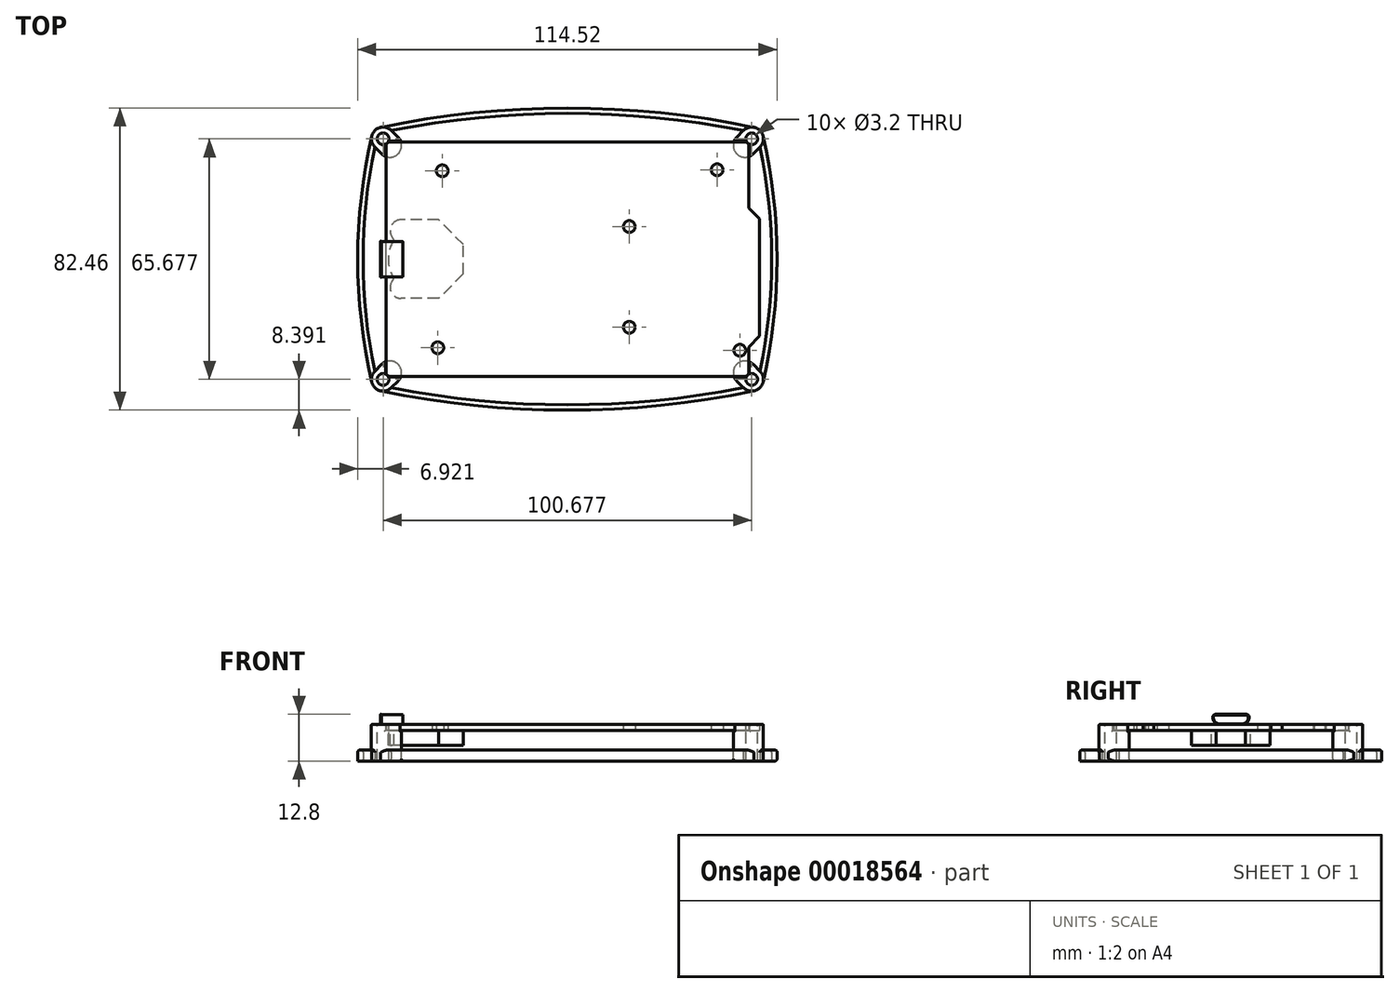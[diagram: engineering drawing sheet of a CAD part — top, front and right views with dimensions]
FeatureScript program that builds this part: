
annotation { "Feature Type Name" : "Feature", "Feature Type Description" : "" }
export const myFeature = defineFeature(function(context is Context, id is Id, definition is map)
    precondition{}
    {
        {
            var Q0;
            Q0=qCreatedBy(makeId("Top.planeOp"),FACE);
            var sketch = newSketch(context, id + "F0", { "sketchPlane" : qUnion([Q0])});
            skLineSegment(sketch, "E0.rect.bottom", {"start": v(48.5, -32) * mm, "end": v(-48.5, -32) * mm});
            skLineSegment(sketch, "E0.rect.top", {"start": v(48.5, 32) * mm, "end": v(-48.5, 32) * mm});
            skLineSegment(sketch, "E0.rect.left", {"start": v(49.5, -31) * mm, "end": v(49.5, -24) * mm});
            skLineSegment(sketch, "E0.rect.right", {"start": v(-49.5, -31) * mm, "end": v(-49.5, 31) * mm});
            skPoint(sketch, "E0.rect.middle", {"position": v(0, 0) * mm});
            skLineSegment(sketch, "E1", {"start": v(49.5, 14) * mm, "end": v(52.5, 11) * mm});
            skLineSegment(sketch, "E2", {"start": v(52.5, 11) * mm, "end": v(52.5, -21) * mm});
            skLineSegment(sketch, "E3", {"start": v(52.5, -21) * mm, "end": v(49.5, -24) * mm});
            skLineSegment(sketch, "E4.trimOffspring", {"start": v(49.5, 14) * mm, "end": v(49.5, 31) * mm});
            skPoint(sketch, "E5.visualSharp", {"position": v(-49.5, 32) * mm});
            skArc(sketch, "E5.filletArc", {"start": v(-48.5, 32) * mm, "mid": v(-49.2, 31.7) * mm, "end": v(-49.5, 31) * mm});
            skPoint(sketch, "E6.visualSharp", {"position": v(49.5, 32) * mm});
            skArc(sketch, "E6.filletArc", {"start": v(49.5, 31) * mm, "mid": v(49.2, 31.7) * mm, "end": v(48.5, 32) * mm});
            skPoint(sketch, "E7.visualSharp", {"position": v(49.5, -32) * mm});
            skArc(sketch, "E7.filletArc", {"start": v(48.5, -32) * mm, "mid": v(49.2, -31.7) * mm, "end": v(49.5, -31) * mm});
            skPoint(sketch, "E8.visualSharp", {"position": v(-49.5, -32) * mm});
            skArc(sketch, "E8.filletArc", {"start": v(-49.5, -31) * mm, "mid": v(-49.2, -31.7) * mm, "end": v(-48.5, -32) * mm});
            skCircle(sketch, "E9", {"center": v(-34.2, 24.1) * mm, "radius": 1.6 * mm});
            skCircle(sketch, "E10", {"center": v(40.9, 24.4) * mm, "radius": 1.6 * mm});
            skCircle(sketch, "E11", {"center": v(47.1, -24.9) * mm, "radius": 1.6 * mm});
            skCircle(sketch, "E12", {"center": v(16.9, -18.6) * mm, "radius": 1.6 * mm});
            skCircle(sketch, "E13", {"center": v(16.9, 8.9) * mm, "radius": 1.6 * mm});
            skCircle(sketch, "E14", {"center": v(-35.4, -24.2) * mm, "radius": 1.6 * mm});
            skSolve(sketch);
        }
        {
            var Q0;
            Q0 = qSketchRegion(id + "F0", true);
            extrude(context, id + "F1", {"entities" : qUnion([Q0]), "depth" : 1.7 * mm});
        }
        {
            var Q0;
            Q0=qCreatedBy(makeId("Right.planeOp"),FACE);
            cPlane(context, id + "F2", {"entities" : qUnion([Q0]), "cplaneType" : CPlaneType.OFFSET, "offset" : 50 * mm, "oppositeDirection" : true, "width" : 150 * mm, "height" : 150 * mm});
        }
        {
            var Q0;
            Q0=qCreatedBy(makeId("Front.planeOp"),FACE);
            var sketch = newSketch(context, id + "F3", { "sketchPlane" : qUnion([Q0])});
            skLineSegment(sketch, "E15", {"start": v(-50.99, 4.41) * mm, "end": v(-50.9, 4.33) * mm});
            skLineSegment(sketch, "E16", {"start": v(-50.83, 4.3) * mm, "end": v(-45, 4.3) * mm});
            skLineSegment(sketch, "E17", {"start": v(-50.91, 4.49) * mm, "end": v(-50.83, 4.4) * mm});
            skLineSegment(sketch, "E18", {"start": v(-50.83, 4.4) * mm, "end": v(-45.1, 4.4) * mm});
            skArc(sketch, "E19", {"start": v(-50.91, 4.49) * mm, "mid": v(-50.99, 4.49) * mm, "end": v(-50.99, 4.41) * mm});
            skPoint(sketch, "E20.visualSharp", {"position": v(-50.87, 4.3) * mm});
            skArc(sketch, "E20.filletArc", {"start": v(-50.9, 4.33) * mm, "mid": v(-50.87, 4.3) * mm, "end": v(-50.83, 4.3) * mm});
            skPoint(sketch, "E21.visualSharp", {"position": v(-45, 4.4) * mm});
            skArc(sketch, "E21.filletArc", {"start": v(-45, 4.3) * mm, "mid": v(-45.03, 4.37) * mm, "end": v(-45.1, 4.4) * mm});
            skSolve(sketch);
        }
        {
            var Q0;
            Q0=qCreatedBy(id+"F2.planeOp",FACE);
            var sketch = newSketch(context, id + "F4", { "sketchPlane" : qUnion([Q0])});
            skPoint(sketch, "E22.0", {"position": v(0, 4.41) * mm});
            skLineSegment(sketch, "E23", {"start": v(0, 4.41) * mm, "end": v(-4.06, 4.41) * mm});
            skArc(sketch, "E24", {"start": v(-4.06, 4.41) * mm, "mid": v(-4.63, 4.18) * mm, "end": v(-4.87, 3.6) * mm});
            skLineSegment(sketch, "E25", {"start": v(0, 4.41) * mm, "end": v(0, 1.7) * mm, "construction": true});
            skLineSegment(sketch, "E26", {"start": v(0, 1.7) * mm, "end": v(-2.98, 1.7) * mm});
            skArc(sketch, "E27", {"start": v(-4.87, 3.6) * mm, "mid": v(-4.32, 2.26) * mm, "end": v(-2.98, 1.7) * mm});
            skLineSegment(sketch, "E28.MirrorCS", {"start": v(0, 4.41) * mm, "end": v(4.06, 4.41) * mm});
            skArc(sketch, "E29.MirrorCS", {"start": v(4.06, 4.41) * mm, "mid": v(4.63, 4.18) * mm, "end": v(4.87, 3.6) * mm});
            skArc(sketch, "E30.MirrorCS", {"start": v(4.87, 3.6) * mm, "mid": v(4.32, 2.26) * mm, "end": v(2.98, 1.7) * mm});
            skLineSegment(sketch, "E31.MirrorCS", {"start": v(0, 1.7) * mm, "end": v(2.98, 1.7) * mm});
            skSolve(sketch);
        }
        {
            var Q0;
            Q0 = qSketchRegion(id + "F3", true);
            var Q1;
            Q1 = qConstructionFilter(qBodyType(qCreatedBy(id + "F4" ,EDGE), BodyType.WIRE), ConstructionObject.NO);
            sweep(context, id + "F5", {"profiles" : qUnion([Q0]), "path" : qUnion([Q1])});
        }
        {
            var Q0;
            Q0=makeQuery(id+"F1.opExtrude","CAP_FACE",FACE,{"disambiguationData":[OSD([sQuery(id+"F0.wireOp",EDGE,"E0.rect.bottom"),sQuery(id+"F0.wireOp",EDGE,"E0.rect.top"),sQuery(id+"F0.wireOp",EDGE,"E0.rect.left"),sQuery(id+"F0.wireOp",EDGE,"E0.rect.right"),sQuery(id+"F0.wireOp",EDGE,"E1"),sQuery(id+"F0.wireOp",EDGE,"E2"),sQuery(id+"F0.wireOp",EDGE,"E3"),sQuery(id+"F0.wireOp",EDGE,"E4.trimOffspring"),sQuery(id+"F0.wireOp",EDGE,"E5.filletArc"),sQuery(id+"F0.wireOp",EDGE,"E6.filletArc"),sQuery(id+"F0.wireOp",EDGE,"E7.filletArc"),sQuery(id+"F0.wireOp",EDGE,"E8.filletArc"),sQuery(id+"F0.wireOp",EDGE,"E9"),sQuery(id+"F0.wireOp",EDGE,"E10"),sQuery(id+"F0.wireOp",EDGE,"E11"),sQuery(id+"F0.wireOp",EDGE,"E12"),sQuery(id+"F0.wireOp",EDGE,"E13"),sQuery(id+"F0.wireOp",EDGE,"E14")])],"isStart":true});
            var sketch = newSketch(context, id + "F6", { "sketchPlane" : qUnion([Q0])});
            skLineSegment(sketch, "E32", {"start": v(0, 0) * mm, "end": v(-125.22, 0) * mm, "construction": true});
            skLineSegment(sketch, "E33", {"start": v(-28.41, 0) * mm, "end": v(-28.41, 4) * mm});
            skLineSegment(sketch, "E34", {"start": v(-28.41, 4) * mm, "end": v(-35.16, 10.75) * mm});
            skLineSegment(sketch, "E35", {"start": v(-35.16, 10.75) * mm, "end": v(-45.41, 10.75) * mm});
            skArc(sketch, "E36", {"start": v(-45.41, 10.75) * mm, "mid": v(-48.1, 9.1) * mm, "end": v(-47.82, 5.96) * mm});
            skArc(sketch, "E37", {"start": v(-47.38, 5.32) * mm, "mid": v(-47.6, 5.64) * mm, "end": v(-47.82, 5.96) * mm});
            skArc(sketch, "E38", {"start": v(-47.38, 5.32) * mm, "mid": v(-48.52, 2.77) * mm, "end": v(-48.91, 0) * mm});
            skArc(sketch, "E39.MirrorCS", {"start": v(-47.38, -5.32) * mm, "mid": v(-47.6, -5.64) * mm, "end": v(-47.82, -5.96) * mm});
            skArc(sketch, "E40.MirrorCS", {"start": v(-47.38, -5.32) * mm, "mid": v(-48.52, -2.77) * mm, "end": v(-48.91, 0) * mm});
            skLineSegment(sketch, "E41.MirrorCS", {"start": v(-28.41, 0) * mm, "end": v(-28.41, -4) * mm});
            skLineSegment(sketch, "E42.MirrorCS", {"start": v(-35.16, -10.75) * mm, "end": v(-45.41, -10.75) * mm});
            skLineSegment(sketch, "E43.MirrorCS", {"start": v(-28.41, -4) * mm, "end": v(-35.16, -10.75) * mm});
            skArc(sketch, "E44.MirrorCS", {"start": v(-45.41, -10.75) * mm, "mid": v(-48.1, -9.1) * mm, "end": v(-47.82, -5.96) * mm});
            skSolve(sketch);
        }
        {
            var Q0;
            Q0 = qSketchRegion(id + "F6", true);
            extrude(context, id + "F7", {"entities" : qUnion([Q0]), "operationType" : NewBodyOperationType.ADD, "depth" : 4 * mm});
        }
        {
            var Q0;
            Q0=makeQuery(id+"F1.opExtrude","CAP_FACE",FACE,{"disambiguationData":[OSD([sQuery(id+"F0.wireOp",EDGE,"E0.rect.bottom"),sQuery(id+"F0.wireOp",EDGE,"E0.rect.top"),sQuery(id+"F0.wireOp",EDGE,"E0.rect.left"),sQuery(id+"F0.wireOp",EDGE,"E0.rect.right"),sQuery(id+"F0.wireOp",EDGE,"E1"),sQuery(id+"F0.wireOp",EDGE,"E2"),sQuery(id+"F0.wireOp",EDGE,"E3"),sQuery(id+"F0.wireOp",EDGE,"E4.trimOffspring"),sQuery(id+"F0.wireOp",EDGE,"E5.filletArc"),sQuery(id+"F0.wireOp",EDGE,"E6.filletArc"),sQuery(id+"F0.wireOp",EDGE,"E7.filletArc"),sQuery(id+"F0.wireOp",EDGE,"E8.filletArc"),sQuery(id+"F0.wireOp",EDGE,"E9"),sQuery(id+"F0.wireOp",EDGE,"E10"),sQuery(id+"F0.wireOp",EDGE,"E11"),sQuery(id+"F0.wireOp",EDGE,"E12"),sQuery(id+"F0.wireOp",EDGE,"E13"),sQuery(id+"F0.wireOp",EDGE,"E14")])],"isStart":false});
            var sketch = newSketch(context, id + "F8", { "sketchPlane" : qUnion([Q0])});
            skCircle(sketch, "E45", {"center": v(50.34, 32.84) * mm, "radius": 1.6 * mm});
            skArc(sketch, "E46", {"start": v(52.6, 30.58) * mm, "mid": v(52.6, 35.1) * mm, "end": v(48.08, 35.1) * mm});
            skArc(sketch, "E47", {"start": v(46.24, 33.26) * mm, "mid": v(46.24, 28.74) * mm, "end": v(50.76, 28.74) * mm});
            skLineSegment(sketch, "E48", {"start": v(46.24, 33.26) * mm, "end": v(48.08, 35.1) * mm});
            skLineSegment(sketch, "E49", {"start": v(52.6, 30.58) * mm, "end": v(50.76, 28.74) * mm});
            skSolve(sketch);
        }
        {
            var Q0;
            Q0 = qSketchRegion(id + "F8", true);
            extrude(context, id + "F9", {"entities" : qUnion([Q0]), "oppositeDirection" : true, "depth" : 10 * mm});
        }
        {
            var Q0;
            Q0=makeQuery(id+"F1.opExtrude","SWEPT_BODY",BODY,{"disambiguationData":[OSD([sQuery(id+"F0.wireOp",EDGE,"E0.rect.bottom"),sQuery(id+"F0.wireOp",EDGE,"E0.rect.top"),sQuery(id+"F0.wireOp",EDGE,"E0.rect.left"),sQuery(id+"F0.wireOp",EDGE,"E0.rect.right"),sQuery(id+"F0.wireOp",EDGE,"E1"),sQuery(id+"F0.wireOp",EDGE,"E2"),sQuery(id+"F0.wireOp",EDGE,"E3"),sQuery(id+"F0.wireOp",EDGE,"E4.trimOffspring"),sQuery(id+"F0.wireOp",EDGE,"E5.filletArc"),sQuery(id+"F0.wireOp",EDGE,"E6.filletArc"),sQuery(id+"F0.wireOp",EDGE,"E7.filletArc"),sQuery(id+"F0.wireOp",EDGE,"E8.filletArc"),sQuery(id+"F0.wireOp",EDGE,"E9"),sQuery(id+"F0.wireOp",EDGE,"E10"),sQuery(id+"F0.wireOp",EDGE,"E11"),sQuery(id+"F0.wireOp",EDGE,"E12"),sQuery(id+"F0.wireOp",EDGE,"E13"),sQuery(id+"F0.wireOp",EDGE,"E14")])]});
            var Q1;
            Q1=makeQuery(id+"F9.opExtrude","SWEPT_BODY",BODY,{"disambiguationData":[OSD([sQuery(id+"F8.wireOp",EDGE,"E45"),sQuery(id+"F8.wireOp",EDGE,"E46"),sQuery(id+"F8.wireOp",EDGE,"E47"),sQuery(id+"F8.wireOp",EDGE,"E48"),sQuery(id+"F8.wireOp",EDGE,"E49")])]});
            var Q2;
            Q2=makeQuery(id+"F1.opExtrude","SWEPT_FACE",FACE,{"disambiguationData":[OSD([sQuery(id+"F0.wireOp",EDGE,"E4.trimOffspring")])]});
            var Q3;
            Q3=makeQuery(id+"F1.opExtrude","SWEPT_FACE",FACE,{"disambiguationData":[OSD([sQuery(id+"F0.wireOp",EDGE,"E0.rect.top")])]});
            var Q4;
            Q4=makeQuery(id+"F1.opExtrude","SWEPT_FACE",FACE,{"disambiguationData":[OSD([sQuery(id+"F0.wireOp",EDGE,"E6.filletArc")])]});
            booleanBodies(context, id + "F10", {"operationType" : BooleanOperationType.SUBTRACTION, "tools" : qUnion([Q0]), "targets" : qUnion([Q1]), "offset" : true, "entitiesToOffset" : qUnion([Q2, Q3, Q4]), "offsetDistance" : 0.2 * mm, "keepTools" : true});
        }
        {
            var Q0;
            Q0=makeQuery(id+"F9.opExtrude","CAP_EDGE",EDGE,{"disambiguationData":[OSD([sQuery(id+"F8.wireOp",EDGE,"E46")])],"isStart":true});
            var Q1;
            Q1=makeQuery(id+"F9.opExtrude","CAP_EDGE",EDGE,{"disambiguationData":[OSD([sQuery(id+"F8.wireOp",EDGE,"E45")])],"isStart":true});
            var Q2;
            Q2=makeQuery(id+"F10.tempBoolean.opBoolean","COPY",EDGE,{"derivedFrom":makeQuery(id+"F10.offsetTempBody.opPattern","COPY",EDGE,{"derivedFrom":makeQuery(id+"F1.opExtrude","CAP_EDGE",EDGE,{"disambiguationData":[OSD([sQuery(id+"F0.wireOp",EDGE,"E4.trimOffspring")])],"isStart":false}),"instanceName":"1"})});
            var Q3;
            Q3=makeQuery(id+"F10.tempBoolean.opBoolean","COPY",EDGE,{"derivedFrom":makeQuery(id+"F10.offsetTempBody.opPattern","COPY",EDGE,{"derivedFrom":makeQuery(id+"F1.opExtrude","CAP_EDGE",EDGE,{"disambiguationData":[OSD([sQuery(id+"F0.wireOp",EDGE,"E0.rect.top")])],"isStart":false}),"instanceName":"1"})});
            var Q4;
            Q4=makeQuery(id+"F10.tempBoolean.opBoolean","INTERSECT",EDGE,{"derivedFrom":[makeQuery(id+"F9.opExtrude","SWEPT_FACE",FACE,{"disambiguationData":[OSD([sQuery(id+"F8.wireOp",EDGE,"E45")])]}),makeQuery(id+"F10.offsetTempBody.opPattern","COPY",FACE,{"derivedFrom":makeQuery(id+"F1.opExtrude","CAP_FACE",FACE,{"disambiguationData":[OSD([sQuery(id+"F0.wireOp",EDGE,"E0.rect.bottom"),sQuery(id+"F0.wireOp",EDGE,"E0.rect.top"),sQuery(id+"F0.wireOp",EDGE,"E0.rect.left"),sQuery(id+"F0.wireOp",EDGE,"E0.rect.right"),sQuery(id+"F0.wireOp",EDGE,"E1"),sQuery(id+"F0.wireOp",EDGE,"E2"),sQuery(id+"F0.wireOp",EDGE,"E3"),sQuery(id+"F0.wireOp",EDGE,"E4.trimOffspring"),sQuery(id+"F0.wireOp",EDGE,"E5.filletArc"),sQuery(id+"F0.wireOp",EDGE,"E6.filletArc"),sQuery(id+"F0.wireOp",EDGE,"E7.filletArc"),sQuery(id+"F0.wireOp",EDGE,"E8.filletArc"),sQuery(id+"F0.wireOp",EDGE,"E9"),sQuery(id+"F0.wireOp",EDGE,"E10"),sQuery(id+"F0.wireOp",EDGE,"E11"),sQuery(id+"F0.wireOp",EDGE,"E12"),sQuery(id+"F0.wireOp",EDGE,"E13"),sQuery(id+"F0.wireOp",EDGE,"E14")])],"isStart":true}),"instanceName":"1"})]});
            var Q5;
            Q5=makeQuery(id+"F10.tempBoolean.opBoolean","INTERSECT",EDGE,{"derivedFrom":[makeQuery(id+"F9.opExtrude","SWEPT_FACE",FACE,{"disambiguationData":[OSD([sQuery(id+"F8.wireOp",EDGE,"E47")])]}),makeQuery(id+"F10.offsetTempBody.opPattern","COPY",FACE,{"derivedFrom":makeQuery(id+"F1.opExtrude","CAP_FACE",FACE,{"disambiguationData":[OSD([sQuery(id+"F0.wireOp",EDGE,"E0.rect.bottom"),sQuery(id+"F0.wireOp",EDGE,"E0.rect.top"),sQuery(id+"F0.wireOp",EDGE,"E0.rect.left"),sQuery(id+"F0.wireOp",EDGE,"E0.rect.right"),sQuery(id+"F0.wireOp",EDGE,"E1"),sQuery(id+"F0.wireOp",EDGE,"E2"),sQuery(id+"F0.wireOp",EDGE,"E3"),sQuery(id+"F0.wireOp",EDGE,"E4.trimOffspring"),sQuery(id+"F0.wireOp",EDGE,"E5.filletArc"),sQuery(id+"F0.wireOp",EDGE,"E6.filletArc"),sQuery(id+"F0.wireOp",EDGE,"E7.filletArc"),sQuery(id+"F0.wireOp",EDGE,"E8.filletArc"),sQuery(id+"F0.wireOp",EDGE,"E9"),sQuery(id+"F0.wireOp",EDGE,"E10"),sQuery(id+"F0.wireOp",EDGE,"E11"),sQuery(id+"F0.wireOp",EDGE,"E12"),sQuery(id+"F0.wireOp",EDGE,"E13"),sQuery(id+"F0.wireOp",EDGE,"E14")])],"isStart":true}),"instanceName":"1"})]});
            var Q6;
            Q6=makeQuery(id+"F10.tempBoolean.opBoolean","INTERSECT",EDGE,{"derivedFrom":[makeQuery(id+"F9.opExtrude","SWEPT_FACE",FACE,{"disambiguationData":[OSD([sQuery(id+"F8.wireOp",EDGE,"E47")])]}),makeQuery(id+"F10.offsetTempBody.opPattern","COPY",FACE,{"derivedFrom":makeQuery(id+"F1.opExtrude","SWEPT_FACE",FACE,{"disambiguationData":[OSD([sQuery(id+"F0.wireOp",EDGE,"E0.rect.top")])]}),"instanceName":"1"})]});
            var Q7;
            Q7=makeQuery(id+"F10.tempBoolean.opBoolean","INTERSECT",EDGE,{"derivedFrom":[makeQuery(id+"F9.opExtrude","SWEPT_FACE",FACE,{"disambiguationData":[OSD([sQuery(id+"F8.wireOp",EDGE,"E47")])]}),makeQuery(id+"F10.offsetTempBody.opPattern","COPY",FACE,{"derivedFrom":makeQuery(id+"F1.opExtrude","SWEPT_FACE",FACE,{"disambiguationData":[OSD([sQuery(id+"F0.wireOp",EDGE,"E4.trimOffspring")])]}),"instanceName":"1"})]});
            var Q8;
            Q8=makeQuery(id+"F9.opExtrude","CAP_EDGE",EDGE,{"disambiguationData":[OSD([sQuery(id+"F8.wireOp",EDGE,"E45")])],"isStart":false});
            var Q9;
            Q9=makeQuery(id+"F10.tempBoolean.opBoolean","INTERSECT",EDGE,{"disambiguationData":[OD(1.0)],"derivedFrom":[makeQuery(id+"F9.opExtrude","SWEPT_FACE",FACE,{"disambiguationData":[OSD([sQuery(id+"F8.wireOp",EDGE,"E45")])]}),makeQuery(id+"F10.offsetTempBody.opPattern","COPY",FACE,{"derivedFrom":makeQuery(id+"F1.opExtrude","SWEPT_FACE",FACE,{"disambiguationData":[OSD([sQuery(id+"F0.wireOp",EDGE,"E6.filletArc")])]}),"instanceName":"1"})]});
            var Q10;
            Q10=makeQuery(id+"F10.tempBoolean.opBoolean","INTERSECT",EDGE,{"disambiguationData":[OD(0.0)],"derivedFrom":[makeQuery(id+"F9.opExtrude","SWEPT_FACE",FACE,{"disambiguationData":[OSD([sQuery(id+"F8.wireOp",EDGE,"E45")])]}),makeQuery(id+"F10.offsetTempBody.opPattern","COPY",FACE,{"derivedFrom":makeQuery(id+"F1.opExtrude","SWEPT_FACE",FACE,{"disambiguationData":[OSD([sQuery(id+"F0.wireOp",EDGE,"E6.filletArc")])]}),"instanceName":"1"})]});
            fillet(context, id + "F11", {"entities" : qUnion([Q0, Q1, Q2, Q3, Q4, Q5, Q6, Q7, Q8, Q9, Q10]), "radius" : 0.25 * mm, "tangentPropagation" : true, "allowEdgeOverflow" : false});
        }
        {
            var Q0;
            Q0=makeQuery(id+"F9.opExtrude","SWEPT_BODY",BODY,{"disambiguationData":[OSD([sQuery(id+"F8.wireOp",EDGE,"E45"),sQuery(id+"F8.wireOp",EDGE,"E46"),sQuery(id+"F8.wireOp",EDGE,"E47"),sQuery(id+"F8.wireOp",EDGE,"E48"),sQuery(id+"F8.wireOp",EDGE,"E49")])]});
            var Q1;
            Q1=qCreatedBy(makeId("Front.planeOp"),FACE);
            mirror(context, id + "F12", {"entities" : qUnion([Q0]), "mirrorPlane" : qUnion([Q1])});
        }
        {
            var Q0;
            Q0=makeQuery(id+"F9.opExtrude","SWEPT_BODY",BODY,{"disambiguationData":[OSD([sQuery(id+"F8.wireOp",EDGE,"E45"),sQuery(id+"F8.wireOp",EDGE,"E46"),sQuery(id+"F8.wireOp",EDGE,"E47"),sQuery(id+"F8.wireOp",EDGE,"E48"),sQuery(id+"F8.wireOp",EDGE,"E49")])]});
            var Q1;
            Q1=makeQuery(id+"F12.opPattern","COPY",BODY,{"derivedFrom":makeQuery(id+"F9.opExtrude","SWEPT_BODY",BODY,{"disambiguationData":[OSD([sQuery(id+"F8.wireOp",EDGE,"E45"),sQuery(id+"F8.wireOp",EDGE,"E46"),sQuery(id+"F8.wireOp",EDGE,"E47"),sQuery(id+"F8.wireOp",EDGE,"E48"),sQuery(id+"F8.wireOp",EDGE,"E49")])]}),"instanceName":"1"});
            var Q2;
            Q2=qCreatedBy(makeId("Right.planeOp"),FACE);
            mirror(context, id + "F13", {"entities" : qUnion([Q0, Q1]), "mirrorPlane" : qUnion([Q2])});
        }
        {
            var Q0;
            Q0=makeQuery(id+"F13.opPattern","COPY",FACE,{"derivedFrom":makeQuery(id+"F9.opExtrude","CAP_FACE",FACE,{"disambiguationData":[OSD([sQuery(id+"F8.wireOp",EDGE,"E45"),sQuery(id+"F8.wireOp",EDGE,"E46"),sQuery(id+"F8.wireOp",EDGE,"E47"),sQuery(id+"F8.wireOp",EDGE,"E48"),sQuery(id+"F8.wireOp",EDGE,"E49")])],"isStart":false}),"instanceName":"1"});
            var sketch = newSketch(context, id + "F14", { "sketchPlane" : qUnion([Q0])});
            skLineSegment(sketch, "E50", {"start": v(0, 0) * mm, "end": v(-22.4, 0) * mm, "construction": true});
            skArc(sketch, "E51", {"start": v(-53.46, 33.55) * mm, "mid": v(-57.26, 0) * mm, "end": v(-53.46, -33.55) * mm});
            skArc(sketch, "E52", {"start": v(-52.6, 30.58) * mm, "mid": v(-55.78, 0) * mm, "end": v(-52.6, -30.58) * mm});
            skLineSegment(sketch, "E53", {"start": v(0, 0) * mm, "end": v(0, 25.87) * mm, "construction": true});
            skArc(sketch, "E54.0", {"start": v(-52.6, -30.58) * mm, "mid": v(-53.41, -31.95) * mm, "end": v(-53.46, -33.55) * mm});
            skArc(sketch, "E55.0", {"start": v(-52.6, 30.58) * mm, "mid": v(-53.41, 31.95) * mm, "end": v(-53.46, 33.55) * mm});
            skSolve(sketch);
        }
        {
            var Q0;
            Q0 = qSketchRegion(id + "F14", true);
            extrude(context, id + "F15", {"entities" : qUnion([Q0]), "oppositeDirection" : true, "depth" : 3 * mm});
        }
        {
            var Q0;
            Q0=makeQuery(id+"F13.opPattern","COPY",FACE,{"derivedFrom":makeQuery(id+"F9.opExtrude","CAP_FACE",FACE,{"disambiguationData":[OSD([sQuery(id+"F8.wireOp",EDGE,"E45"),sQuery(id+"F8.wireOp",EDGE,"E46"),sQuery(id+"F8.wireOp",EDGE,"E47"),sQuery(id+"F8.wireOp",EDGE,"E48"),sQuery(id+"F8.wireOp",EDGE,"E49")])],"isStart":false}),"instanceName":"1"});
            var sketch = newSketch(context, id + "F16", { "sketchPlane" : qUnion([Q0])});
            skLineSegment(sketch, "E56", {"start": v(0, 0) * mm, "end": v(-17.58, 0) * mm, "construction": true});
            skLineSegment(sketch, "E57", {"start": v(0, 14.8) * mm, "end": v(0, 0) * mm, "construction": true});
            skArc(sketch, "E58", {"start": v(51, 35.97) * mm, "mid": v(0, 41.23) * mm, "end": v(-51, 35.97) * mm});
            skArc(sketch, "E59", {"start": v(48.08, 35.1) * mm, "mid": v(0, 39.8) * mm, "end": v(-48.08, 35.1) * mm});
            skArc(sketch, "E60.0", {"start": v(-51, 35.97) * mm, "mid": v(-49.42, 35.9) * mm, "end": v(-48.08, 35.1) * mm});
            skArc(sketch, "E61.0", {"start": v(51, 35.97) * mm, "mid": v(49.42, 35.9) * mm, "end": v(48.08, 35.1) * mm});
            skSolve(sketch);
        }
        {
            var Q0;
            Q0 = qSketchRegion(id + "F16", true);
            extrude(context, id + "F17", {"entities" : qUnion([Q0]), "oppositeDirection" : true, "depth" : 3 * mm});
        }
        {
            var Q0;
            Q0=makeQuery(id+"F15.opExtrude","SWEPT_BODY",BODY,{"disambiguationData":[OSD([sQuery(id+"F14.wireOp",EDGE,"E51"),sQuery(id+"F14.wireOp",EDGE,"E52"),sQuery(id+"F14.wireOp",EDGE,"E54.0"),sQuery(id+"F14.wireOp",EDGE,"E55.0")])]});
            var Q1;
            Q1=qCreatedBy(makeId("Right.planeOp"),FACE);
            mirror(context, id + "F18", {"entities" : qUnion([Q0]), "mirrorPlane" : qUnion([Q1])});
        }
        {
            var Q0;
            Q0=makeQuery(id+"F17.opExtrude","SWEPT_BODY",BODY,{"disambiguationData":[OSD([sQuery(id+"F16.wireOp",EDGE,"E58"),sQuery(id+"F16.wireOp",EDGE,"E59"),sQuery(id+"F16.wireOp",EDGE,"E60.0"),sQuery(id+"F16.wireOp",EDGE,"E61.0")])]});
            var Q1;
            Q1=qCreatedBy(makeId("Front.planeOp"),FACE);
            mirror(context, id + "F19", {"entities" : qUnion([Q0]), "mirrorPlane" : qUnion([Q1])});
        }
        {
            var Q0;
            Q0=makeQuery(id+"F18.opPattern","COPY",EDGE,{"derivedFrom":makeQuery(id+"F15.opExtrude","CAP_EDGE",EDGE,{"disambiguationData":[OSD([sQuery(id+"F14.wireOp",EDGE,"E51")])],"isStart":true}),"instanceName":"1"});
            var Q1;
            Q1=makeQuery(id+"F19.opPattern","COPY",EDGE,{"derivedFrom":makeQuery(id+"F17.opExtrude","CAP_EDGE",EDGE,{"disambiguationData":[OSD([sQuery(id+"F16.wireOp",EDGE,"E59")])],"isStart":true}),"instanceName":"1"});
            var Q2;
            Q2=makeQuery(id+"F9.opExtrude","CAP_EDGE",EDGE,{"disambiguationData":[OSD([sQuery(id+"F8.wireOp",EDGE,"E48")])],"isStart":false});
            var Q3;
            Q3=makeQuery(id+"F18.opPattern","COPY",EDGE,{"derivedFrom":makeQuery(id+"F15.opExtrude","CAP_EDGE",EDGE,{"disambiguationData":[OSD([sQuery(id+"F14.wireOp",EDGE,"E52")])],"isStart":true}),"instanceName":"1"});
            var Q4;
            Q4=makeQuery(id+"F12.opPattern","COPY",EDGE,{"derivedFrom":makeQuery(id+"F9.opExtrude","CAP_EDGE",EDGE,{"disambiguationData":[OSD([sQuery(id+"F8.wireOp",EDGE,"E49")])],"isStart":false}),"instanceName":"1"});
            var Q5;
            Q5=makeQuery(id+"F17.opExtrude","CAP_EDGE",EDGE,{"disambiguationData":[OSD([sQuery(id+"F16.wireOp",EDGE,"E59")])],"isStart":true});
            var Q6;
            Q6=makeQuery(id+"F13.opPattern","COPY",EDGE,{"derivedFrom":makeQuery(id+"F12.opPattern","COPY",EDGE,{"derivedFrom":makeQuery(id+"F9.opExtrude","CAP_EDGE",EDGE,{"disambiguationData":[OSD([sQuery(id+"F8.wireOp",EDGE,"E48")])],"isStart":false}),"instanceName":"1"}),"instanceName":"1"});
            var Q7;
            Q7=makeQuery(id+"F15.opExtrude","CAP_EDGE",EDGE,{"disambiguationData":[OSD([sQuery(id+"F14.wireOp",EDGE,"E52")])],"isStart":true});
            var Q8;
            Q8=makeQuery(id+"F13.opPattern","COPY",EDGE,{"derivedFrom":makeQuery(id+"F9.opExtrude","CAP_EDGE",EDGE,{"disambiguationData":[OSD([sQuery(id+"F8.wireOp",EDGE,"E49")])],"isStart":false}),"instanceName":"1"});
            var Q9;
            Q9=makeQuery(id+"F17.opExtrude","CAP_EDGE",EDGE,{"disambiguationData":[OSD([sQuery(id+"F16.wireOp",EDGE,"E58")])],"isStart":false});
            var Q10;
            Q10=makeQuery(id+"F17.opExtrude","CAP_EDGE",EDGE,{"disambiguationData":[OSD([sQuery(id+"F16.wireOp",EDGE,"E59")])],"isStart":false});
            var Q11;
            Q11=makeQuery(id+"F15.opExtrude","CAP_EDGE",EDGE,{"disambiguationData":[OSD([sQuery(id+"F14.wireOp",EDGE,"E51")])],"isStart":false});
            var Q12;
            Q12=makeQuery(id+"F15.opExtrude","CAP_EDGE",EDGE,{"disambiguationData":[OSD([sQuery(id+"F14.wireOp",EDGE,"E52")])],"isStart":false});
            var Q13;
            Q13=makeQuery(id+"F18.opPattern","COPY",EDGE,{"derivedFrom":makeQuery(id+"F15.opExtrude","CAP_EDGE",EDGE,{"disambiguationData":[OSD([sQuery(id+"F14.wireOp",EDGE,"E52")])],"isStart":false}),"instanceName":"1"});
            var Q14;
            Q14=makeQuery(id+"F18.opPattern","COPY",EDGE,{"derivedFrom":makeQuery(id+"F15.opExtrude","CAP_EDGE",EDGE,{"disambiguationData":[OSD([sQuery(id+"F14.wireOp",EDGE,"E51")])],"isStart":false}),"instanceName":"1"});
            var Q15;
            Q15=makeQuery(id+"F19.opPattern","COPY",EDGE,{"derivedFrom":makeQuery(id+"F17.opExtrude","CAP_EDGE",EDGE,{"disambiguationData":[OSD([sQuery(id+"F16.wireOp",EDGE,"E59")])],"isStart":false}),"instanceName":"1"});
            var Q16;
            Q16=makeQuery(id+"F19.opPattern","COPY",EDGE,{"derivedFrom":makeQuery(id+"F17.opExtrude","CAP_EDGE",EDGE,{"disambiguationData":[OSD([sQuery(id+"F16.wireOp",EDGE,"E58")])],"isStart":false}),"instanceName":"1"});
            fillet(context, id + "F20", {"entities" : qUnion([Q0, Q1, Q2, Q3, Q4, Q5, Q6, Q7, Q8, Q9, Q10, Q11, Q12, Q13, Q14, Q15, Q16]), "radius" : 0.6 * mm, "tangentPropagation" : true, "allowEdgeOverflow" : false});
        }
    });
